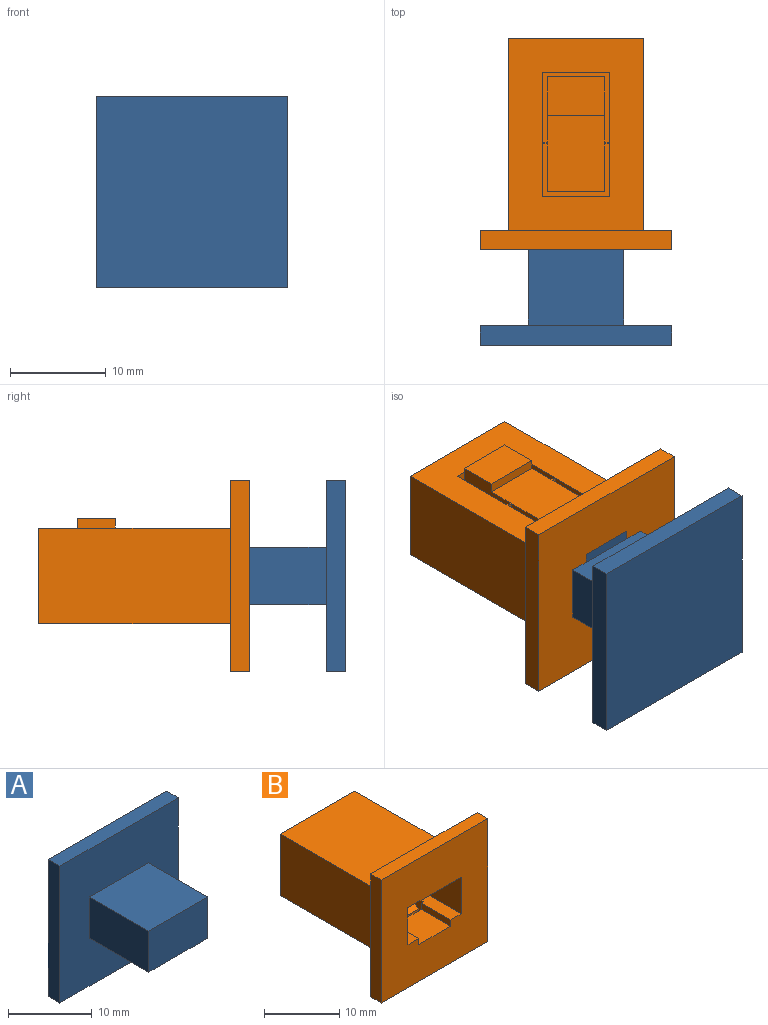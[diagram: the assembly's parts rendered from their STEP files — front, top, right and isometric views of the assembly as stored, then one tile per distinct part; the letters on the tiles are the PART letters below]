
ASSEMBLY  parts=2 mates=1
PART A: 15 faces, bbox 20x12x20 mm
  f0: plane 10x10mm, normal (0,0,-1), area 88mm2, adj f1,f3,f4,f10,f11,f12,f13
  f1: plane 10x6mm, normal (1,0,0), area 60mm2, adj f0,f2,f4,f10
  f2: plane 10x10mm, normal (0,0,1), area 100mm2, adj f1,f3,f4,f10
  f3: plane 10x6mm, normal (-1,0,0), area 60mm2, adj f0,f2,f4,f10
  f4: plane 10x6mm, normal (0,-1,0), area 60mm2, adj f0,f1,f2,f3,f14
  f5: plane 20x2mm, normal (-1,0,0), area 40mm2, adj f6,f8,f9,f10
  f6: plane 20x2mm, normal (0,0,-1), area 40mm2, adj f5,f7,f9,f10
  f7: plane 20x2mm, normal (1,0,0), area 40mm2, adj f6,f8,f9,f10
  f8: plane 20x2mm, normal (0,0,1), area 40mm2, adj f5,f7,f9,f10
  f9: plane 20x20mm, normal (0,1,0), area 400mm2, adj f5,f6,f7,f8
  f10: plane 20x20mm, normal (0,-1,0), area 340mm2, adj f0,f1,f2,f3,f5,f6,f7,f8
  f11: plane 6x1mm, normal (0,1,0), area 6mm2, adj f0,f12,f13,f14
  f12: plane 2x1mm, normal (-1,0,0), area 1mm2, adj f0,f11,f14
  f13: plane 2x1mm, normal (1,0,0), area 1mm2, adj f0,f11,f14
  f14: plane 6x2mm, normal (0,-0.45,-0.89), area 13.4mm2, adj f4,f11,f12,f13
PART B: 41 faces, bbox 20x22x20 mm
  f0: plane 22x2mm, normal (0,0,1), area 37.5mm2, adj f5,f7,f8,f19,f20,f25,f35,f36
  f1: plane 20x14mm, normal (0,0,-1), area 237.2mm2, adj f8,f9,f14,f16,f23,f24,f25,f26
  f2: plane 3.5x1mm, normal (1,0,0), area 3.5mm2, adj f4,f6,f8,f25
  f3: plane 10x7mm, normal (0,0,1), area 60.2mm2, adj f23,f24,f26,f27,f28,f29,f30,f31
  f4: plane 6x3.5mm, normal (0,0,1), area 21mm2, adj f2,f5,f8,f25
  f5: plane 3.5x1mm, normal (-1,0,0), area 3.5mm2, adj f0,f4,f8,f25
  f6: plane 22x2mm, normal (0,0,1), area 37.5mm2, adj f2,f7,f8,f17,f22,f25,f34,f36
  f7: plane 20x20mm, normal (0,-1,0), area 334mm2, adj f0,f6,f10,f11,f12,f13,f17,f18
  f8: plane 14x10mm, normal (0,1,0), area 74mm2, adj f0,f1,f2,f4,f5,f6,f14,f15
  f9: plane 20x20mm, normal (0,1,0), area 260mm2, adj f1,f10,f11,f12,f13,f14,f15,f16
  f10: plane 20x2mm, normal (0,0,-1), area 40mm2, adj f7,f9,f11,f13
  f11: plane 20x2mm, normal (1,0,0), area 40mm2, adj f7,f9,f10,f12
  f12: plane 20x2mm, normal (0,0,1), area 40mm2, adj f7,f9,f11,f13
  f13: plane 20x2mm, normal (-1,0,0), area 40mm2, adj f7,f9,f10,f12
  f14: plane 20x10mm, normal (1,0,0), area 200mm2, adj f1,f8,f9,f15
  f15: plane 20x14mm, normal (0,0,1), area 280mm2, adj f8,f9,f14,f16
  f16: plane 20x10mm, normal (-1,0,0), area 200mm2, adj f1,f8,f9,f15
  f17: plane 5.5x1mm, normal (1,0,0), area 5.5mm2, adj f6,f7,f18,f36
  f18: plane 6x5.5mm, normal (0,0,1), area 33mm2, adj f7,f17,f19,f36
  f19: plane 5.5x1mm, normal (-1,0,0), area 5.5mm2, adj f0,f7,f18,f36
  f20: plane 22x6mm, normal (-1,0,0), area 132mm2, adj f0,f7,f8,f21
  f21: plane 22x10mm, normal (0,0,-1), area 220mm2, adj f7,f8,f20,f22
  f22: plane 22x6mm, normal (1,0,0), area 132mm2, adj f6,f7,f8,f21
  f23: plane 6.8x2mm, normal (-1,0,0), area 10.8mm2, adj f1,f3,f27,f28,f37,f38
  f24: plane 6.8x2mm, normal (1,0,0), area 10.8mm2, adj f1,f3,f26,f28,f37,f38
  f25: plane 7x2mm, normal (0,-1,0), area 8mm2, adj f0,f1,f2,f4,f5,f6,f34,f35
  f26: plane 1x0.5mm, normal (0,1,0), area 0.5mm2, adj f1,f3,f24,f35
  f27: plane 1x0.5mm, normal (0,1,0), area 0.5mm2, adj f1,f3,f23,f34
  f28: plane 6x2mm, normal (0,1,0), area 12mm2, adj f3,f23,f24,f38
  f29: plane 5x2mm, normal (1,0,0), area 5.8mm2, adj f1,f3,f32,f33,f39,f40
  f30: plane 5x2mm, normal (-1,0,0), area 5.8mm2, adj f1,f3,f31,f32,f39,f40
  f31: plane 1x0.5mm, normal (0,-1,0), area 0.5mm2, adj f1,f3,f30,f34
  f32: plane 6x0.8mm, normal (0,-1,0), area 4.8mm2, adj f1,f29,f30,f40
  f33: plane 1x0.5mm, normal (0,-1,0), area 0.5mm2, adj f1,f3,f29,f35
  f34: plane 13x2mm, normal (1,0,0), area 25.8mm2, adj f1,f3,f6,f25,f27,f31,f36
  f35: plane 13x2mm, normal (-1,0,0), area 25.8mm2, adj f0,f1,f3,f25,f26,f33,f36
  f36: plane 7x2mm, normal (0,1,0), area 8mm2, adj f0,f1,f6,f17,f18,f19,f34,f35
  f37: plane 6x1mm, normal (0,-1,0), area 6mm2, adj f1,f23,f24,f38
  f38: plane 6x4mm, normal (0,0,-1), area 24mm2, adj f23,f24,f28,f37
  f39: plane 6x1mm, normal (0,1,0), area 6mm2, adj f3,f29,f30,f40
  f40: plane 6x2mm, normal (0,-0.51,0.86), area 14mm2, adj f29,f30,f32,f39
PLACE A rot(axis=(-1,0,0),180deg) t=(-0.35,-13.7,9.92)mm
PLACE B rot(axis=(0,1,0),180deg) t=(-0.35,-3.7,9.92)mm fixed
MATE slider A.f10 <-> B.f7  axis (0,1,0) through (4.65,-13.7,12.92)mm
